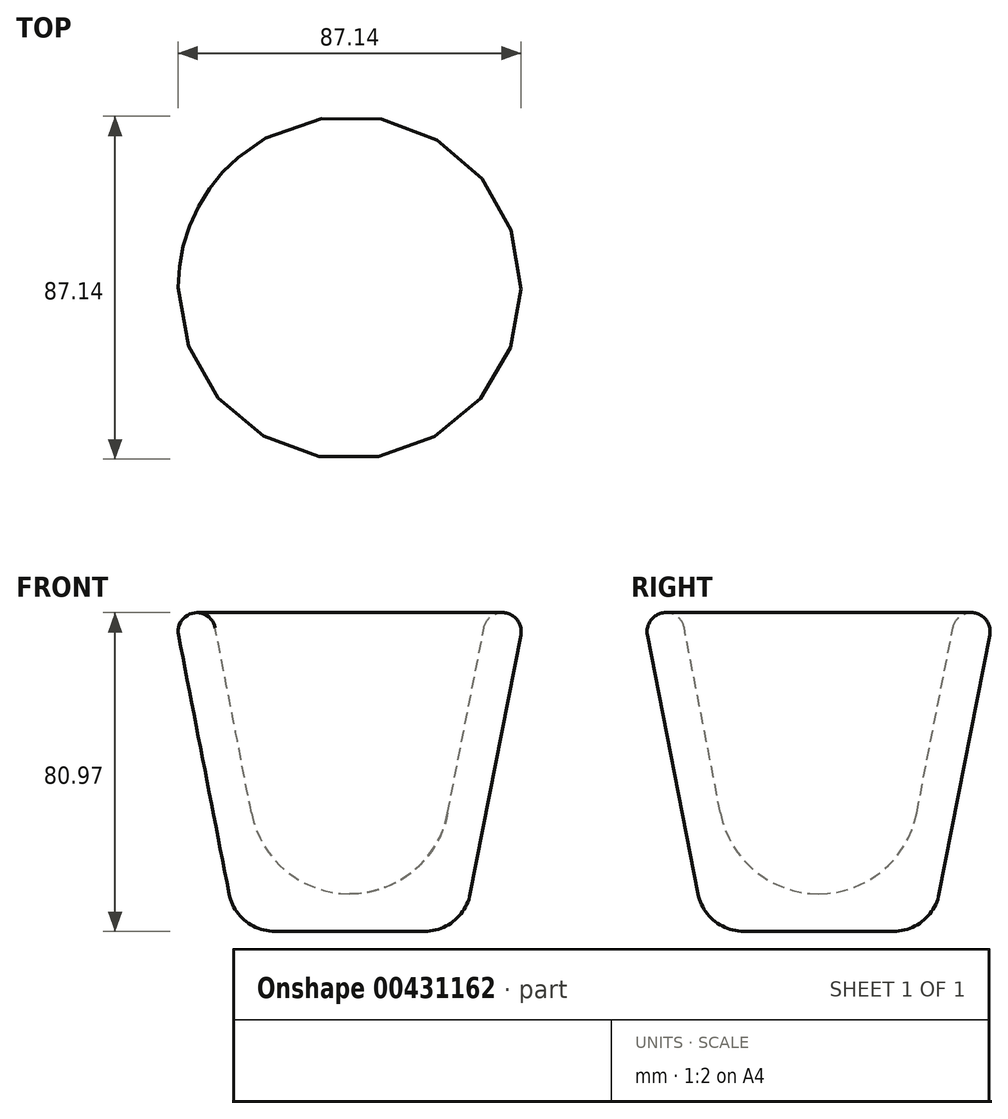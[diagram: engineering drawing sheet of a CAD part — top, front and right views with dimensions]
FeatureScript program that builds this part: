
annotation { "Feature Type Name" : "Feature", "Feature Type Description" : "" }
export const myFeature = defineFeature(function(context is Context, id is Id, definition is map)
    precondition{}
    {
        {
            var Q0;
            Q0=qCreatedBy(makeId("Front.planeOp"),FACE);
            var sketch = newSketch(context, id + "F0", { "sketchPlane" : qUnion([Q0])});
            skArc(sketch, "E0", {"start": v(0, 0) * mm, "mid": v(16.14, 5.8) * mm, "end": v(24.93, 20.52) * mm});
            skLineSegment(sketch, "E1", {"start": v(24.93, 20.52) * mm, "end": v(34.13, 67.59) * mm});
            skArc(sketch, "E2", {"start": v(43.48, 65.76) * mm, "mid": v(39.72, 71.35) * mm, "end": v(34.13, 67.59) * mm});
            skLineSegment(sketch, "E3", {"start": v(43.48, 65.76) * mm, "end": v(30.62, 0) * mm});
            skLineSegment(sketch, "E4", {"start": v(0, -9.53) * mm, "end": v(0, 0) * mm});
            skLineSegment(sketch, "E5", {"start": v(0, -9.53) * mm, "end": v(19.05, -9.53) * mm});
            skArc(sketch, "E6", {"start": v(19.05, -9.53) * mm, "mid": v(26.54, -6.84) * mm, "end": v(30.62, 0) * mm});
            skLineSegment(sketch, "E7", {"start": v(0, 0) * mm, "end": v(-24.53, 0) * mm, "construction": true});
            skSolve(sketch);
        }
        {
            var Q0;
            Q0 = qSketchRegion(id + "F0", true);
            var Q1;
            Q1=sQuery(id+"F0.wireOp",EDGE,"E4");
            revolve(context, id + "F1", {"entities" : qUnion([Q0]), "axis" : qUnion([Q1]), "revolveType" : RevolveType.FULL});
        }
    });
